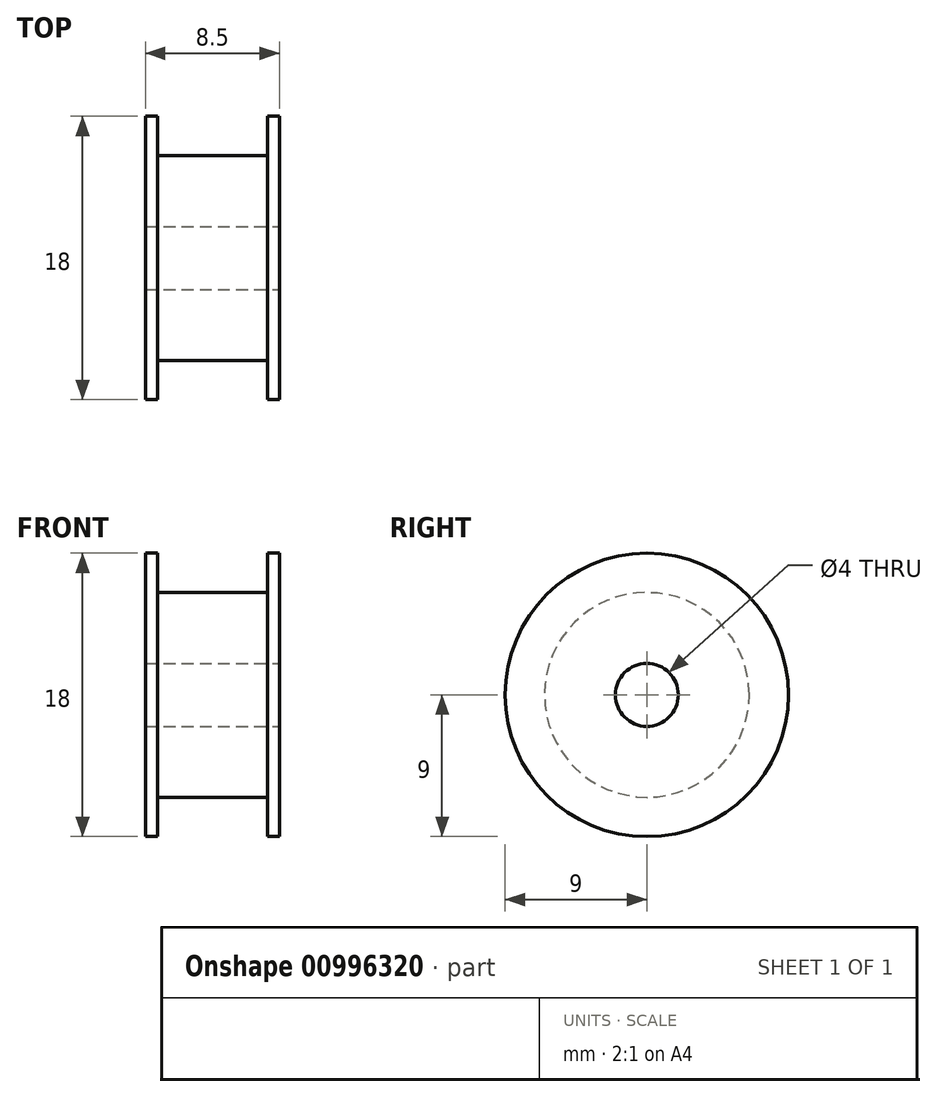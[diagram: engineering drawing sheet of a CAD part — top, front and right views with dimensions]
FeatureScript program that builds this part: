
annotation { "Feature Type Name" : "Feature", "Feature Type Description" : "" }
export const myFeature = defineFeature(function(context is Context, id is Id, definition is map)
    precondition{}
    {
        {
            var Q0;
            Q0=qCreatedBy(makeId("Right.planeOp"),FACE);
            var sketch = newSketch(context, id + "F0", { "sketchPlane" : qUnion([Q0])});
            skCircle(sketch, "E0", {"center": v(0, 0) * mm, "radius": 9 * mm, "construction": true});
            skCircle(sketch, "E1.0", {"center": v(0, 0) * mm, "radius": 6.5 * mm});
            skSolve(sketch);
        }
        {
            var Q0;
            Q0 = qSketchRegion(id + "F0", true);
            extrude(context, id + "F1", {"entities" : qUnion([Q0]), "depth" : 3.5 * mm, "offsetDistance" : 25 * mm, "hasSecondDirection" : true, "secondDirectionOppositeDirection" : true, "secondDirectionDepth" : 3.5 * mm});
        }
        {
            var Q0;
            Q0=makeQuery(id+"F1.opExtrude","CAP_FACE",FACE,{"disambiguationData":[OSD([sQuery(id+"F0.wireOp",EDGE,"E1.0")])],"isStart":false});
            var sketch = newSketch(context, id + "F2", { "sketchPlane" : qUnion([Q0])});
            skCircle(sketch, "E2", {"center": v(0, 0) * mm, "radius": 9 * mm});
            skSolve(sketch);
        }
        {
            var Q0;
            Q0 = qSketchRegion(id + "F2", true);
            extrude(context, id + "F3", {"entities" : qUnion([Q0]), "operationType" : NewBodyOperationType.ADD, "depth" : (1.5 / 2) * mm, "offsetDistance" : 25 * mm});
        }
        {
            var Q0;
            Q0=makeQuery(id+"F1.opExtrude","CAP_FACE",FACE,{"disambiguationData":[OSD([sQuery(id+"F0.wireOp",EDGE,"E1.0")])],"isStart":true});
            var sketch = newSketch(context, id + "F4", { "sketchPlane" : qUnion([Q0])});
            skCircle(sketch, "E3.0", {"center": v(0, 0) * mm, "radius": 9 * mm});
            skSolve(sketch);
        }
        {
            var Q0;
            Q0 = qSketchRegion(id + "F4", true);
            extrude(context, id + "F5", {"entities" : qUnion([Q0]), "operationType" : NewBodyOperationType.ADD, "depth" : (1.5 / 2) * mm, "offsetDistance" : 25 * mm});
        }
        {
            var Q0;
            Q0=qCreatedBy(makeId("Right.planeOp"),FACE);
            var sketch = newSketch(context, id + "F6", { "sketchPlane" : qUnion([Q0])});
            skCircle(sketch, "E4", {"center": v(0, 0) * mm, "radius": 2 * mm});
            skSolve(sketch);
        }
        {
            var Q0;
            Q0 = qSketchRegion(id + "F6", true);
            extrude(context, id + "F7", {"entities" : qUnion([Q0]), "operationType" : NewBodyOperationType.REMOVE, "oppositeDirection" : true, "depth" : 25 * mm, "offsetDistance" : 25 * mm, "hasSecondDirection" : true, "secondDirectionOppositeDirection" : false, "secondDirectionDepth" : 25 * mm});
        }
    });
